# Revit family: NBS_Allermuir_OffcChrs_Cardita_Stool
name_source: partatom
category: Furniture
revit_build: Autodesk Revit 2018 (Build: 20190510_1515(x64)
units: mm (PartAtom-declared; Revit-internal decimal feet)

## family parameters
Always vertical = Yes
Cut with Voids When Loaded = No
Room Calculation Point = No
Shared = No
Work Plane-Based = No

## types (2) — shared parameters
AssetType = Movable
Category = Pr_40_50_12_57:Office chairs
Color = Solid Ash, White Oak stain, American Cherry stain, American Walnut stain, Dark Walnut stain, Wenge stain, White as Snow colour wash, Back to Black colour wash, Slate Grey colour wash, Smoke Grey colour wash, Vintage Red colour wash, Ruby Red colour wash, Fern Green colour wash, Peacock Green colour wash, Blue Skies colour wash, Sapphire Blue colour wash, Orange Crush colour wash, Mellow Yellow colour wash, Nut Brown colour wash, Turtle Dove colour wash, Sherbert Yellow colour wash, Blush Pink colour wash
Description = High stool on wood legs
DurationUnit = year
ExpectedLife = 10
Features = Molded shell, Fully upholstered with luxury quilt detail, Solid Ash legs with a clear finish, Footrest finished in Polished Chrome, Plastic glides, Solid Ash legs can be stained or colorwashed, Plastic glides with felt
Finish = Clear Solid Ash
FootrestMaterial = NBS_Allermuir_Chrome_Polished
FrameFinish = Clear
FrameMaterial = Solid Ash
IfcExportAs = IfcFurnitureType
IfcExportType = STOOL
IsBuiltIn = No
LegMaterial = NBS_Allermuir_Ash_ClearFinish
ManufacturerName = Allermuir
ManufacturerURL = www.allermuir.co.uk
Material = Fabric, PU Foam, Steel, Solid Wood
ModelReference = Cardita_Stool
NBSCertification = www.nationalbimlibrary.com/cert/kbuej2ep
NBSDescription = Office chairs
NBSReference = 45-35-20/330
NominalDepth = 515 mm
NominalHeight = 1010 mm
NominalLength = 500 mm  [stored 1.64042 ft]
NominalWidth = 500 mm  [stored 1.64042 ft]
ProductInformation = https://www.allermuir.com
SeatDepth = 370 mm
SeatMaterial = NBS_Allermuir_Fabric
SeatWidth = 435 mm
Status = UNSET
Style = Stool
SustainabilityPerformance = 99% recyclable
Uniclass2015Code = Pr_40_50_12_57
Uniclass2015Title = Office chairs
Uniclass2015Version = Products v1.15
Version = 1
WarrantyDescription = Allermuir warrant that its manufactured products are free from manufacturing defects - in materials or workmanship - for a period of five (5) years. , Allermuir will repair, or replace (at Allermuir's sole discretion) with comparable free of charge materials / components, any product / component which fails under normal use in a single shift environment, as a result of a defect in the materials and/ or workmanship
WarrantyDurationParts = 5
WarrantyDurationUnit = year
WoodStains = White Oak, American Cherry, American Walnut, Dark walnut, Wenge
zero-valued in all types: HighestSeatingHeight, LowestSeatingHeight

## per-type parameters (varying)
| type | BIMObjectName | FootrestHeight | ModelNumber | Name | SeatingHeight | Size |
| Cardita_Stool_CRD03 | NBS_Allermuir_OfficeChairs_Cardita_Stool_CRD03 | 273 mm | CRD03 | OfficeChairs_CRD03_Cardita_Allermuir | 730 mm | 515 x 1010 x 500 mm |
| Cardita_Stool_CRD03CH | NBS_Allermuir_OfficeChairs_Cardita_Stool_CRD03CH | 232 mm | CRD03CH | OfficeChairs_CRD03CH_Cardita_Allermuir | 605 mm | 515 x 885 x 500 mm |

note: [stored X ft] marks values corroborated as IEEE doubles in the binary element streams (Revit-internal decimal feet)

## geometry (parser evidence)
native form markers: Sweep x5
no freeform markers — native parametric forms only
